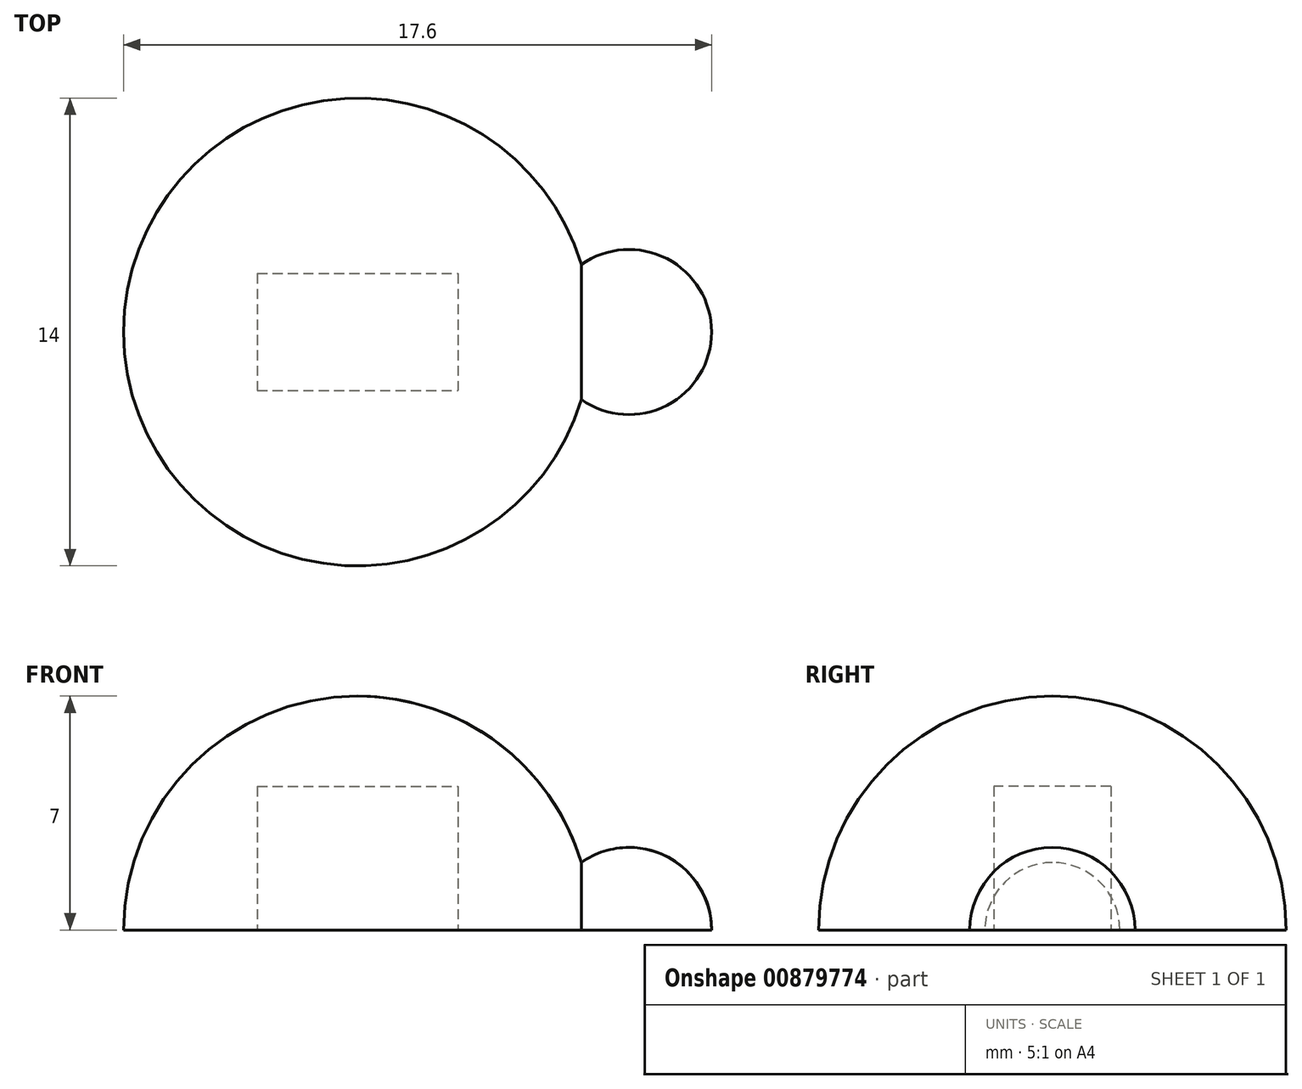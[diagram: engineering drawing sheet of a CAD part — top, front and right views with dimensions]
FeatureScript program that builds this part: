
annotation { "Feature Type Name" : "Feature", "Feature Type Description" : "" }
export const myFeature = defineFeature(function(context is Context, id is Id, definition is map)
    precondition{}
    {
        {
            var Q0;
            Q0=qCreatedBy(makeId("Front.planeOp"),FACE);
            var sketch = newSketch(context, id + "F0", { "sketchPlane" : qUnion([Q0])});
            skLineSegment(sketch, "E0", {"start": v(0, 0) * mm, "end": v(7, 0) * mm});
            skArc(sketch, "E1", {"start": v(7, 0) * mm, "mid": v(4.95, 4.95) * mm, "end": v(0, 7) * mm});
            skLineSegment(sketch, "E2", {"start": v(0, 0) * mm, "end": v(0, 7) * mm});
            skSolve(sketch);
        }
        {
            var Q0;
            Q0=makeQuery(id+"F0.imprint","IMPRINT",FACE,{"disambiguationData":[TD([[makeQuery(id+"F0.imprint","IMPRINT",EDGE,{"derivedFrom":sQuery(id+"F0.wireOp",EDGE,"E0")}),1.0]])]});
            var Q1;
            Q1=sQuery(id+"F0.wireOp",EDGE,"E2");
            revolve(context, id + "F1", {"surfaceOperationType" : NewSurfaceOperationType.NEW, "entities" : qUnion([Q0]), "axis" : qUnion([Q1]), "revolveType" : RevolveType.FULL});
        }
        {
            var Q0;
            Q0=qCreatedBy(makeId("Front.planeOp"),FACE);
            var sketch = newSketch(context, id + "F2", { "sketchPlane" : qUnion([Q0])});
            skArc(sketch, "E3", {"start": v(10.6, 0) * mm, "mid": v(9.87, 1.75) * mm, "end": v(8.13, 2.47) * mm});
            skLineSegment(sketch, "E4", {"start": v(8.13, 0) * mm, "end": v(8.13, 2.47) * mm});
            skLineSegment(sketch, "E5", {"start": v(8.13, 0) * mm, "end": v(10.6, 0) * mm});
            skSolve(sketch);
        }
        {
            var Q0;
            Q0=makeQuery(id+"F2.imprint","IMPRINT",FACE,{"disambiguationData":[TD([[makeQuery(id+"F2.imprint","IMPRINT",EDGE,{"derivedFrom":sQuery(id+"F2.wireOp",EDGE,"E3")}),1.0]])]});
            var Q1;
            Q1=sQuery(id+"F2.wireOp",EDGE,"E4");
            revolve(context, id + "F3", {"operationType" : NewBodyOperationType.ADD, "surfaceOperationType" : NewSurfaceOperationType.NEW, "entities" : qUnion([Q0]), "axis" : qUnion([Q1]), "revolveType" : RevolveType.FULL});
        }
        {
            var Q0;
            Q0=qCreatedBy(makeId("Top.planeOp"),FACE);
            var sketch = newSketch(context, id + "F4", { "sketchPlane" : qUnion([Q0])});
            skLineSegment(sketch, "E6.bottom", {"start": v(-3, 1.75) * mm, "end": v(3, 1.75) * mm});
            skLineSegment(sketch, "E6.top", {"start": v(-3, -1.75) * mm, "end": v(3, -1.75) * mm});
            skLineSegment(sketch, "E6.left", {"start": v(-3, 1.75) * mm, "end": v(-3, -1.75) * mm});
            skLineSegment(sketch, "E6.right", {"start": v(3, 1.75) * mm, "end": v(3, -1.75) * mm});
            skPoint(sketch, "E6.middle", {"position": v(0, 0) * mm});
            skSolve(sketch);
        }
        {
            var Q0;
            Q0=makeQuery(id+"F4.imprint","IMPRINT",FACE,{"disambiguationData":[TD([[makeQuery(id+"F4.imprint","IMPRINT",EDGE,{"derivedFrom":sQuery(id+"F4.wireOp",EDGE,"E6.bottom")}),-1.0]])]});
            extrude(context, id + "F5", {"entities" : qUnion([Q0]), "operationType" : NewBodyOperationType.REMOVE, "depth" : 4.3 * mm, "offsetDistance" : 25 * mm});
        }
    });
